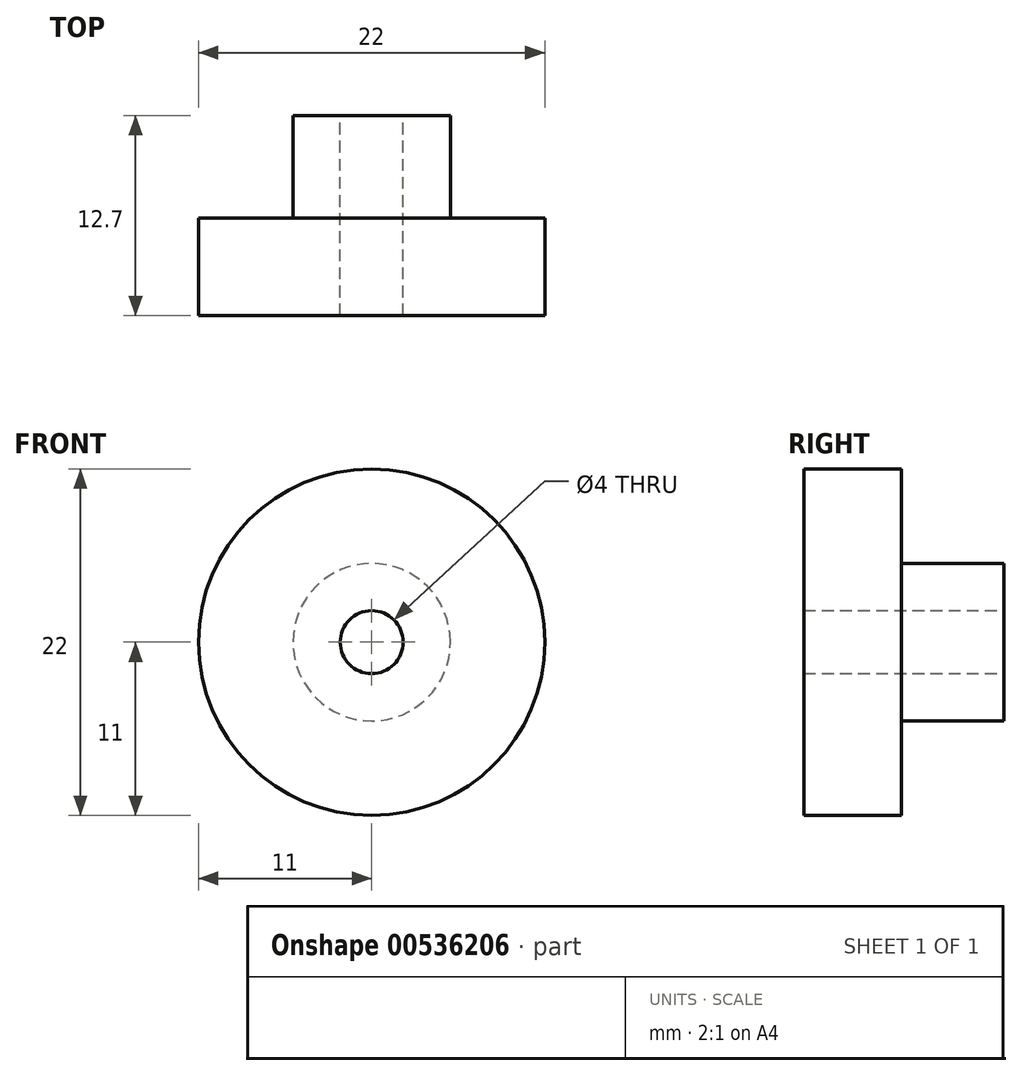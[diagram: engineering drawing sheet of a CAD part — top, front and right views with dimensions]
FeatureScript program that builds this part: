
annotation { "Feature Type Name" : "Feature", "Feature Type Description" : "" }
export const myFeature = defineFeature(function(context is Context, id is Id, definition is map)
    precondition{}
    {
        {
            var Q0;
            Q0=qCreatedBy(makeId("Front.planeOp"),FACE);
            var sketch = newSketch(context, id + "F0", { "sketchPlane" : qUnion([Q0])});
            skCircle(sketch, "E0", {"center": v(0, 0) * mm, "radius": 11 * mm});
            skSolve(sketch);
        }
        {
            var Q0;
            Q0=makeQuery(id+"F0.imprint","IMPRINT",FACE,{"disambiguationData":[TD([[makeQuery(id+"F0.imprint","IMPRINT",EDGE,{"derivedFrom":sQuery(id+"F0.wireOp",EDGE,"E0")}),1.0]])]});
            extrude(context, id + "F1", {"entities" : qUnion([Q0]), "depth" : 6.2 * mm, "offsetDistance" : 25 * mm});
        }
        {
            var Q0;
            Q0=makeQuery(id+"F1.opExtrude","CAP_FACE",FACE,{"disambiguationData":[OSD([sQuery(id+"F0.wireOp",EDGE,"E0")])],"isStart":true});
            var sketch = newSketch(context, id + "F2", { "sketchPlane" : qUnion([Q0])});
            skCircle(sketch, "E1", {"center": v(0, 0) * mm, "radius": 5 * mm});
            skSolve(sketch);
        }
        {
            var Q0;
            Q0=makeQuery(id+"F2.imprint","IMPRINT",FACE,{"disambiguationData":[TD([[makeQuery(id+"F2.imprint","IMPRINT",EDGE,{"derivedFrom":sQuery(id+"F2.wireOp",EDGE,"E1")}),1.0]])]});
            extrude(context, id + "F3", {"entities" : qUnion([Q0]), "operationType" : NewBodyOperationType.ADD, "depth" : 6.5 * mm, "offsetDistance" : 25 * mm});
        }
        {
            var Q0;
            Q0=makeQuery(id+"F3.opExtrude","CAP_FACE",FACE,{"disambiguationData":[OSD([sQuery(id+"F2.wireOp",EDGE,"E1")])],"isStart":false});
            var sketch = newSketch(context, id + "F4", { "sketchPlane" : qUnion([Q0])});
            skCircle(sketch, "E2", {"center": v(0, 0) * mm, "radius": 2 * mm});
            skSolve(sketch);
        }
        {
            var Q0;
            Q0=makeQuery(id+"F4.imprint","IMPRINT",FACE,{"disambiguationData":[TD([[makeQuery(id+"F4.imprint","IMPRINT",EDGE,{"derivedFrom":sQuery(id+"F4.wireOp",EDGE,"E2")}),1.0]])]});
            extrude(context, id + "F5", {"entities" : qUnion([Q0]), "operationType" : NewBodyOperationType.REMOVE, "oppositeDirection" : true, "depth" : 25 * mm, "offsetDistance" : 25 * mm});
        }
    });
